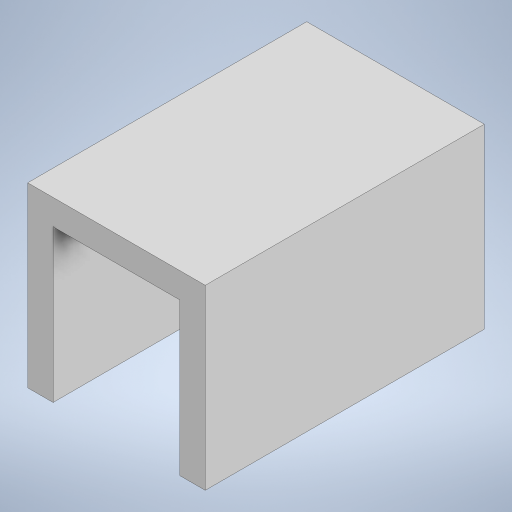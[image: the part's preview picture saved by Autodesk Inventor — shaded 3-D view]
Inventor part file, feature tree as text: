
AUTODESK INVENTOR PART (.ipt)
format: ipt  version: 2023 (Build 270158000, 158)  size: 169,472 bytes
history: native  units: in
note: dims shown in document units (in); Inventor stores cm internally (conversion verified against a paired STEP export)
features: extrude x2, sketch x2
ambient origin geometry x8: Origin, YZ Plane, XZ Plane, XY Plane, X Axis, Y Axis, Z Axis, Center Point
bodies: Solid1 (feature_tree)
feature tree (4):
  extrude  "Extrusion1"  Depth=0.5512in
  extrude  "Extrusion2"  Depth=0.3937in
  sketch  "Sketch1"  dims[d0=0.5512in d1=0.5512in]
  sketch  "Sketch2"  dims[d2=0.8661in d3=0.0in d4=0.3937in d5=0.7874in d6=0.7874in d7=0.0in]
